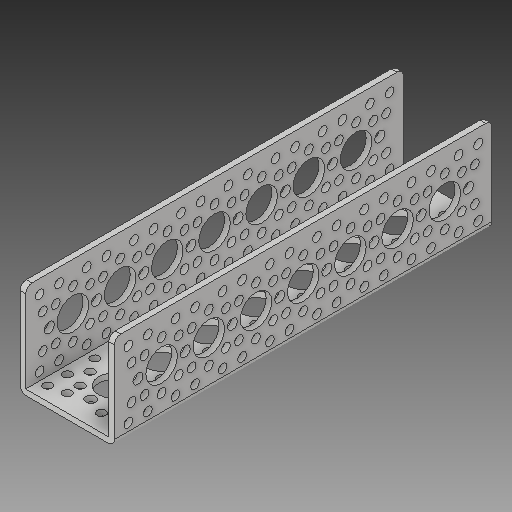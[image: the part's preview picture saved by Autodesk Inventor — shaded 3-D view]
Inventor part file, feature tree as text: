
AUTODESK INVENTOR PART (.ipt)
format: ipt  version: 2017 (Build 210142000, 142)  size: 501,248 bytes
history: native  units: in
note: dims shown in document units (in); Inventor stores cm internally (conversion verified against a paired STEP export)
features: fillet x1
ambient origin geometry x8: Origin, YZ Plane, XZ Plane, XY Plane, X Axis, Y Axis, Z Axis, Center Point
bodies: Solid1 (feature_tree)
feature tree (1):
  fillet  "Fillet1"  [1 undecoded]
note: 1 required parameter value undecoded (feature->parameter linkage not recoverable at this tier; creation-order binding heuristic only, values carry confidence <= 0.55)
